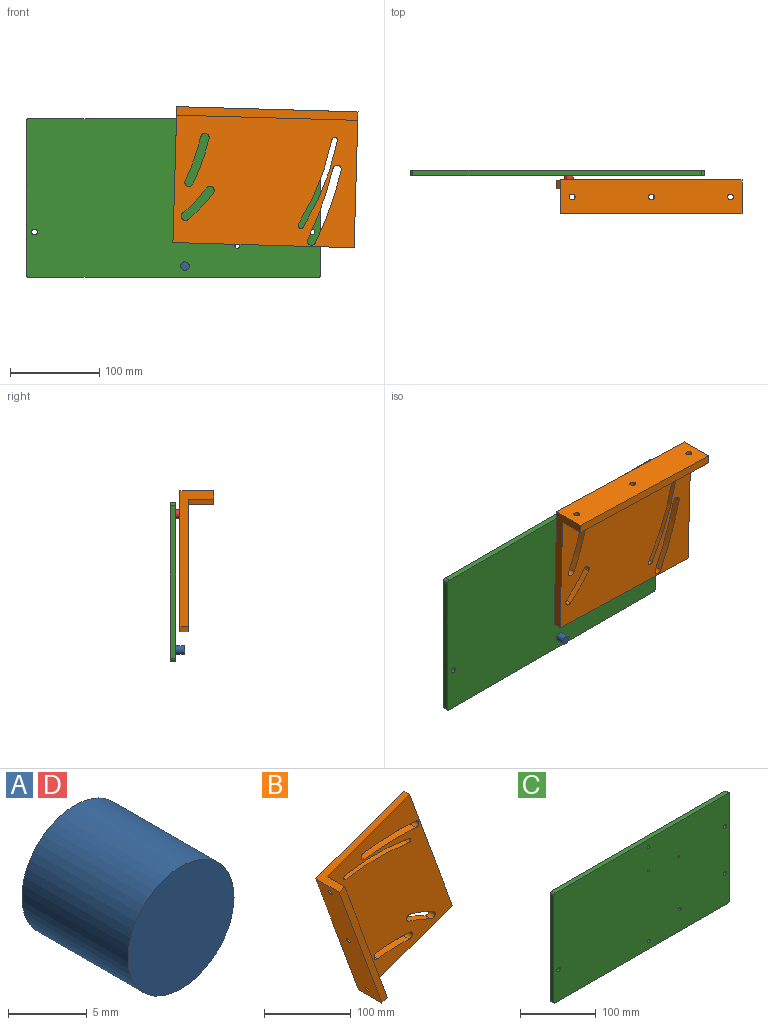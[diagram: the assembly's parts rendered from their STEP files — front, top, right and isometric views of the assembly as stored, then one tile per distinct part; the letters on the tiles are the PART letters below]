
ASSEMBLY  parts=4 mates=5
PART A: 3 faces, bbox 9.5x9.5x9.5 mm
  f0: cylinder r=4.76mm len=9.53mm, axis (0,1,0), area 285mm2, adj f1,f2
  f1: plane 9.53x9.53mm, normal (0,-1,0), area 71.3mm2, adj f0
  f2: plane 9.53x9.53mm, normal (0,1,0), area 71.3mm2, adj f0
PART B: 27 faces, bbox 212.7x38.1x243.1 mm
  f0: plane 239.81x203.76mm, normal (0,-1,0), area 26429.8mm2, adj f1,f2,f3,f4,f5,f6,f7,f8
  f1: cylinder r=401.64mm len=83.91mm, axis (0,1,0), area 801.2mm2, adj f0,f2,f20,f21
  f2: cylinder r=4.76mm len=9.53mm, axis (0,1,0), area 142.5mm2, adj f0,f1,f3,f21
  f3: cylinder r=411.16mm len=85.9mm, axis (0,1,0), area 820.2mm2, adj f0,f2,f20,f21
  f4: cylinder r=249.24mm len=52.07mm, axis (0,1,0), area 497.2mm2, adj f0,f5,f16,f21
  f5: cylinder r=4.76mm len=9.53mm, axis (0,1,0), area 142.5mm2, adj f0,f4,f6,f21
  f6: cylinder r=258.76mm len=54.06mm, axis (0,1,0), area 516.2mm2, adj f0,f5,f16,f21
  f7: cylinder r=185.74mm len=36mm, axis (0,1,0), area 370.5mm2, adj f0,f8,f17,f21
  f8: cylinder r=4.76mm len=9.53mm, axis (0,1,0), area 142.5mm2, adj f0,f7,f9,f21
  f9: cylinder r=195.26mm len=37.85mm, axis (0,1,0), area 389.5mm2, adj f0,f8,f17,f21
  f10: cylinder r=293.68mm len=101.99mm, axis (0,1,0), area 976.4mm2, adj f0,f11,f18,f21
  f11: cylinder r=3.18mm len=9.53mm, axis (0,1,0), area 95.2mm2, adj f0,f10,f12,f21
  f12: cylinder r=300.04mm len=104.2mm, axis (0,1,0), area 997.6mm2, adj f0,f11,f18,f21
  f13: plane 190.95x69.5mm, normal (0.94,0,0.34), area 1935.5mm2, adj f0,f14,f19,f21
  f14: plane 143.21x52.12mm, normal (-0.34,0,0.94), area 1723.8mm2, adj f0,f13,f15,f21,f22,f23
  f15: plane 190.95x69.5mm, normal (-0.94,0,-0.34), area 7641.5mm2, adj f14,f19,f21,f23,f24,f25,f26
  f16: cylinder r=4.76mm len=9.53mm, axis (0,1,0), area 142.5mm2, adj f0,f4,f6,f21
  f17: cylinder r=4.76mm len=9.53mm, axis (0,1,0), area 142.5mm2, adj f0,f7,f9,f21
  f18: cylinder r=3.18mm len=9.53mm, axis (0,1,0), area 95.2mm2, adj f0,f10,f12,f21
  f19: plane 143.21x52.12mm, normal (0.34,0,-0.94), area 1723.8mm2, adj f0,f13,f15,f21,f22,f23
  f20: cylinder r=4.76mm len=9.53mm, axis (0,1,0), area 142.5mm2, adj f0,f1,f3,f21
  f21: plane 243.07x212.71mm, normal (0,1,0), area 28365.3mm2, adj f1,f2,f3,f4,f5,f6,f7,f8
  f22: plane 190.95x69.5mm, normal (0.94,0,0.34), area 5706mm2, adj f0,f14,f19,f23,f24,f25,f26
  f23: plane 194.2x78.45mm, normal (0,-1,0), area 1935.5mm2, adj f14,f15,f19,f22
  f24: cylinder r=3.26mm len=11.18mm, axis (0.94,0,0.34), area 195.3mm2, adj f15,f22
  f25: cylinder r=3.26mm len=11.18mm, axis (0.94,0,0.34), area 195.3mm2, adj f15,f22
  f26: cylinder r=3.26mm len=11.18mm, axis (0.94,0,0.34), area 195.3mm2, adj f15,f22
PART C: 18 faces, bbox 330.2x6.4x177.8 mm
  f0: plane 323.85x6.35mm, normal (0,0,1), area 2056.4mm2, adj f1,f15,f16,f17
  f1: cylinder r=3.17mm len=6.35mm, axis (0,1,0), area 31.7mm2, adj f0,f2,f16,f17
  f2: plane 171.45x6.35mm, normal (-1,0,0), area 1088.7mm2, adj f1,f3,f16,f17
  f3: cylinder r=3.17mm len=6.35mm, axis (0,1,0), area 31.7mm2, adj f2,f4,f16,f17
  f4: plane 323.85x6.35mm, normal (0,0,-1), area 2056.4mm2, adj f3,f5,f16,f17
  f5: cylinder r=3.17mm len=6.35mm, axis (0,1,0), area 31.7mm2, adj f4,f6,f16,f17
  f6: plane 171.45x6.35mm, normal (1,0,0), area 1088.7mm2, adj f5,f15,f16,f17
  f7: cylinder r=2.54mm len=6.35mm, axis (0,1,0), area 101.3mm2, adj f16,f17
  f8: cylinder r=2.54mm len=6.35mm, axis (0,1,0), area 101.3mm2, adj f16,f17
  f9: cylinder r=3.26mm len=6.53mm, axis (0,1,0), area 130.2mm2, adj f16,f17
  f10: cylinder r=3.26mm len=6.53mm, axis (0,1,0), area 130.2mm2, adj f16,f17
  f11: cylinder r=3.26mm len=6.53mm, axis (0,1,0), area 130.2mm2, adj f16,f17
  f12: cylinder r=2.02mm len=6.35mm, axis (0,1,0), area 80.6mm2, adj f16,f17
  f13: cylinder r=2.02mm len=6.35mm, axis (0,1,0), area 80.6mm2, adj f16,f17
  f14: cylinder r=2.55mm len=6.35mm, axis (0,1,0), area 101.8mm2, adj f16,f17
  f15: cylinder r=3.17mm len=6.35mm, axis (0,1,0), area 31.7mm2, adj f0,f6,f16,f17
  f16: plane 330.2x177.8mm, normal (0,-1,0), area 58513.9mm2, adj f0,f1,f2,f3,f4,f5,f6,f7
  f17: plane 330.2x177.8mm, normal (0,1,0), area 58513.9mm2, adj f0,f1,f2,f3,f4,f5,f6,f7
PART D: same geometry as A
PLACE A rot(axis=(1,0,0),180deg) t=(-108.14,31.26,105.81)mm
PLACE B rot(axis=(0,1,0),111.6deg) t=(-231.07,36.02,306.78)mm
PLACE C t=(-286.43,47.13,93.11)mm fixed
PLACE D t=(-108.63,40.78,258.21)mm
MATE slider C.f7 <-> A.f0  axis (0,-1,0) through (-108.14,40.78,105.81)mm
MATE pin_slot D.f0 <-> B.f7  axis (0,-1,0) through (-108.63,31.26,258.21)mm
MATE planar A.f0 <-> C.f16  axis (0,1,0) through (-108.14,40.78,105.81)mm
MATE slider D.f0 <-> C.f8  axis (0,-1,0) through (-108.63,31.26,258.21)mm
MATE planar D.f0 <-> C.f9  axis (0,1,0) through (-108.63,40.78,258.21)mm
